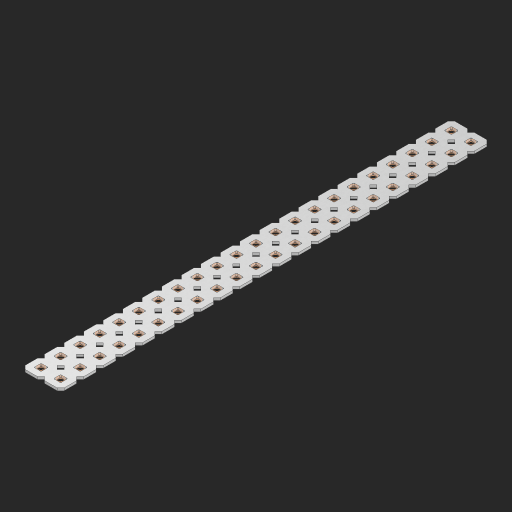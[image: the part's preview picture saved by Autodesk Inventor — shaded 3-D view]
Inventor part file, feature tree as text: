
AUTODESK INVENTOR PART (.ipt)
format: ipt  version: 2023 (Build 270158000, 158)  size: 781,312 bytes
history: native  units: in
note: dims shown in document units (in); Inventor stores cm internally (conversion verified against a paired STEP export)
features: other x45, extrude x43, sketch x2, pattern_linear x1
ambient origin geometry x8: Origin, YZ Plane, XZ Plane, XY Plane, X Axis, Y Axis, Z Axis, Center Point
bodies: Solid1 (feature_tree), Body (feature_tree)
feature tree (91):
  pattern_linear  "Rectangular Pattern1"  Spacing1=0.09in  [1 undecoded]
  sketch  "Sketch1"  dims[d1=0.5in]
  sketch  "Sketch2"  dims[d2=0.182in d3=0.09in d4=0.09in d5=0.09in d6=0.09in d7=0.09in d8=0.09in d9=0.09in d10=0.09in d11=0.02in d13=0.0in d14=0.172in d15=0.0625in d16=0.0in d19=0.5in d22=0.5in]
  other  "Srf1"
  other  "Srf126"
  other  "Srf127"
  other  "Srf128"
  other  "Srf129"
  other  "Srf130"
  other  "Srf131"
  other  "Srf250"
  other  "Srf251"
  other  "Srf252"
  other  "Srf253"
  other  "Srf254"
  other  "Srf255"
  other  "Srf256"
  other  "Srf257"
  other  "Srf258"
  other  "Srf259"
  other  "Srf260"
  other  "Srf261"
  other  "Srf262"
  other  "Srf263"
  other  "Srf264"
  other  "Srf268"
  other  "Srf269"
  other  "Srf270"
  other  "Srf271"
  other  "Srf272"
  other  "Srf273"
  other  "Srf274"
  other  "Srf275"
  other  "Srf276"
  other  "Srf277"
  other  "Srf278"
  other  "Srf279"
  other  "Srf280"
  other  "Srf281"
  other  "Srf282"
  other  "Srf283"
  other  "Srf284"
  other  "Srf285"
  other  "Srf286"
  other  "Srf287"
  other  "Srf288"
  other  "Srf289"
  other  "Circle"
  extrude  "ExtrusionSrf126"  Depth=0.09in
  extrude  "ExtrusionSrf127"  Depth=0.09in
  extrude  "ExtrusionSrf128"  Depth=0.09in
  extrude  "ExtrusionSrf129"  Depth=0.09in
  extrude  "ExtrusionSrf130"  Depth=0.09in
  extrude  "ExtrusionSrf131"  Depth=0.09in
  extrude  "ExtrusionSrf250"  Depth=0.09in
  extrude  "ExtrusionSrf251"  Depth=0.02in
  extrude  "ExtrusionSrf252"  TaperAngle=0.0deg  [1 undecoded]
  extrude  "ExtrusionSrf253"  Depth=0.5in
  extrude  "ExtrusionSrf254"  Depth=0.0625in TaperAngle=0.0deg
  extrude  "ExtrusionSrf255"  Depth=0.5in
  extrude  "ExtrusionSrf256"  Depth=0.5in
  extrude  "ExtrusionSrf257"  [1 undecoded]
  extrude  "ExtrusionSrf258"  [1 undecoded]
  extrude  "ExtrusionSrf259"  [1 undecoded]
  extrude  "ExtrusionSrf260"  [1 undecoded]
  extrude  "ExtrusionSrf261"  [1 undecoded]
  extrude  "ExtrusionSrf262"  [1 undecoded]
  extrude  "ExtrusionSrf263"  [1 undecoded]
  extrude  "ExtrusionSrf264"  [1 undecoded]
  extrude  "ExtrusionSrf268"  [1 undecoded]
  extrude  "ExtrusionSrf269"  [1 undecoded]
  extrude  "ExtrusionSrf270"  [1 undecoded]
  extrude  "ExtrusionSrf271"  [1 undecoded]
  extrude  "ExtrusionSrf272"  [1 undecoded]
  extrude  "ExtrusionSrf273"  [1 undecoded]
  extrude  "ExtrusionSrf274"  [1 undecoded]
  extrude  "ExtrusionSrf275"  [1 undecoded]
  extrude  "ExtrusionSrf276"  [1 undecoded]
  extrude  "ExtrusionSrf277"  [1 undecoded]
  extrude  "ExtrusionSrf278"  [1 undecoded]
  extrude  "ExtrusionSrf279"  [1 undecoded]
  extrude  "ExtrusionSrf280"  [1 undecoded]
  extrude  "ExtrusionSrf281"  [1 undecoded]
  extrude  "ExtrusionSrf282"  [1 undecoded]
  extrude  "ExtrusionSrf283"  [1 undecoded]
  extrude  "ExtrusionSrf284"  [1 undecoded]
  extrude  "ExtrusionSrf285"  [1 undecoded]
  extrude  "ExtrusionSrf286"  [1 undecoded]
  extrude  "ExtrusionSrf287"  [1 undecoded]
  extrude  "ExtrusionSrf288"  [1 undecoded]
  extrude  "ExtrusionSrf289"  [1 undecoded]
note: 32 required parameter values undecoded (feature->parameter linkage not recoverable at this tier; creation-order binding heuristic only, values carry confidence <= 0.55)
